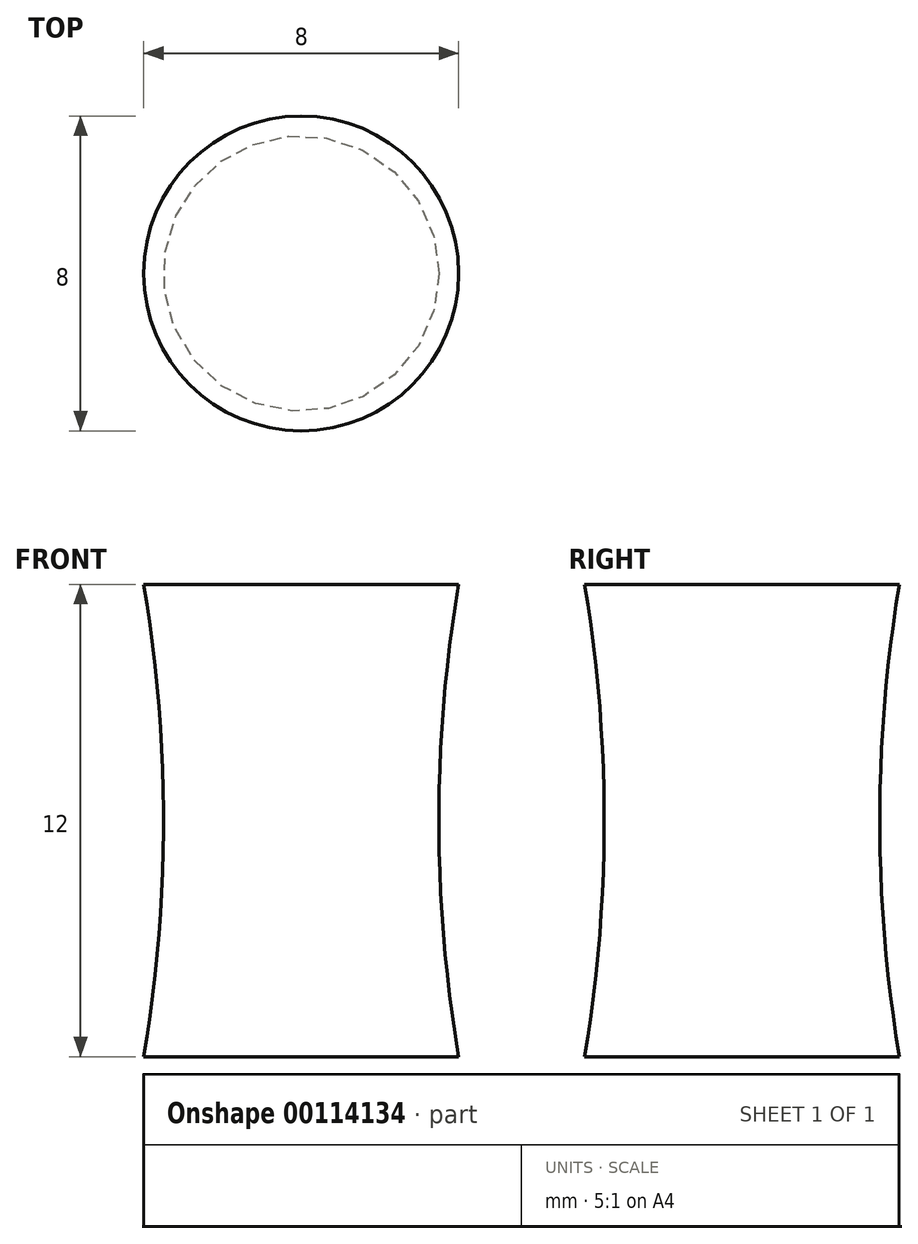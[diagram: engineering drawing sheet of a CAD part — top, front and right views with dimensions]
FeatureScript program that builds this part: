
annotation { "Feature Type Name" : "Feature", "Feature Type Description" : "" }
export const myFeature = defineFeature(function(context is Context, id is Id, definition is map)
    precondition{}
    {
        {
            var Q0;
            Q0=qCreatedBy(makeId("Front.planeOp"),FACE);
            var sketch = newSketch(context, id + "F0", { "sketchPlane" : qUnion([Q0])});
            skArc(sketch, "E0", {"start": v(-4, -6) * mm, "mid": v(-3.5, 0) * mm, "end": v(-4, 6) * mm});
            skLineSegment(sketch, "E1", {"start": v(0, 6) * mm, "end": v(0, -6) * mm});
            skLineSegment(sketch, "E2", {"start": v(370.3, 0) * mm, "end": v(0, 0) * mm});
            skLineSegment(sketch, "E3", {"start": v(-4, 6) * mm, "end": v(0, 6) * mm});
            skLineSegment(sketch, "E4", {"start": v(-4, -6) * mm, "end": v(0, -6) * mm});
            skSolve(sketch);
        }
        {
            var Q0;
            Q0=makeQuery(id+"F0.imprint","IMPRINT",FACE,{"disambiguationData":[TD([[makeQuery(id+"F0.imprint","IMPRINT",EDGE,{"derivedFrom":sQuery(id+"F0.wireOp",EDGE,"E0")}),-1.0]])]});
            var Q1;
            Q1=sQuery(id+"F0.wireOp",EDGE,"E1");
            revolve(context, id + "F1", {"entities" : qUnion([Q0]), "axis" : qUnion([Q1]), "revolveType" : RevolveType.FULL});
        }
    });
